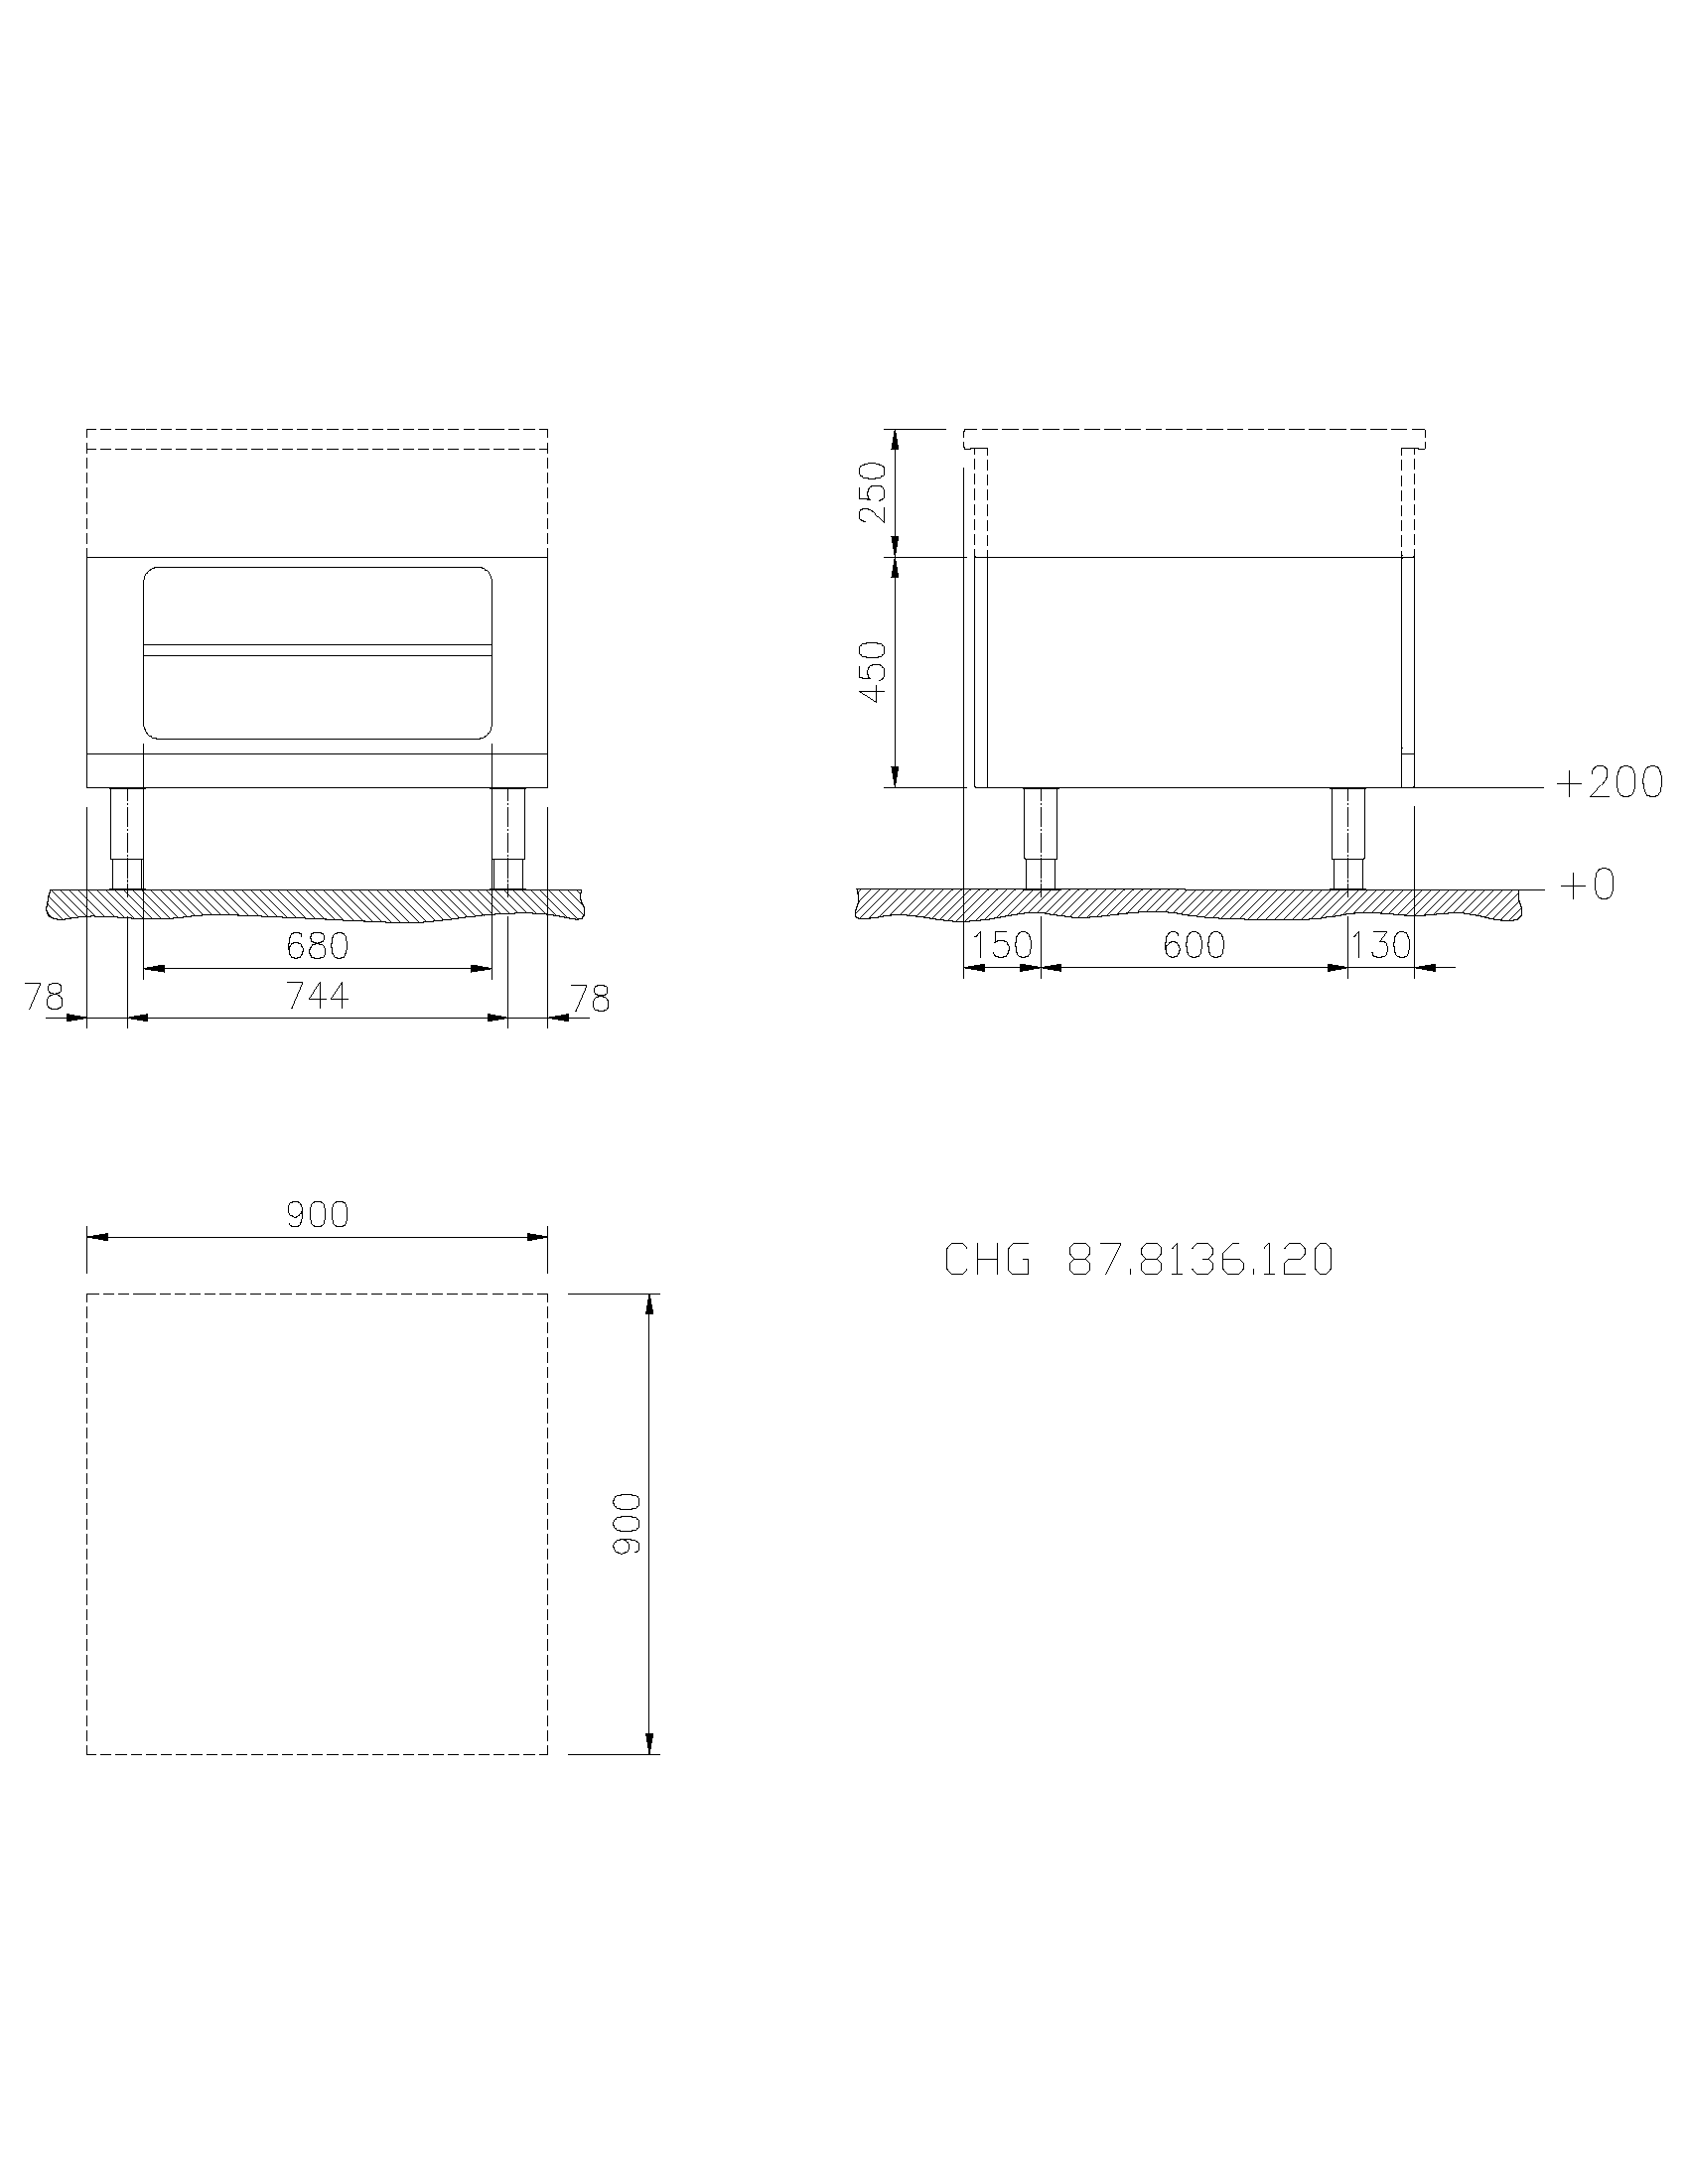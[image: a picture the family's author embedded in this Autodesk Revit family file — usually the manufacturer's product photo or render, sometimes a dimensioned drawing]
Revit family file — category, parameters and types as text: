
# Revit family: QF_ELECTROLUXPROFESSIONAL_589865_MCKCEADDDM
name_source: partatom
category: Specialty Equipment
units: mm (PartAtom-declared; Revit-internal decimal feet)

## family parameters
Always vertical = Yes
Cut with Voids When Loaded = No
Enable Cutting in Views = No
Maintain Annotation Orientation = No
Part Type = Normal
Room Calculation Point = No
Round Connector Dimension = Use Diameter
Shared = No
Work Plane-Based = No

## types (1)
- Standard
    Accessory = No
    Cold Water Size = 1"
    Compressed Air Pressure = 0.00 psi
    Compressed Air Size = 0"
    Compressed Air Volume = 0 GPM
    Condensate Return Size = 0"
    Cycle = 50 Hz
    Default Elevation = 0 mm  [stored 0 ft]
    Depth Actual = 900 mm  [stored 2.95276 ft]
    Description = PASTA COOKER, 1X24,5L, 1-SIDE, 400X900X700H-MARINE
    Direct Waste Size = 1"
    Gas Input Pressure = 0.0
    Gas KW = 0
    Gas Size = 0"
    HP = 8 HP
    Height Actual = 700 mm  [stored 2.29659 ft]
    Hot Water Size = 0"
    Item Number = 589865
    Length Actual = 400 mm  [stored 1.31234 ft]
    Manufacturer = Electrolux Professional
    Model = MCKCEADDDM
    Phase = 3
    Refrigerant Compressor Remote = Yes
    Refrigeration Liquid Line Size = 0 mm  [stored 0 ft]
    Refrigeration Suction Line Size = 0 mm  [stored 0 ft]
    Steam Consumption per Hour = 0
    Steam Supply Maximum Pressure = 0.00 psi
    Steam Supply Minimum Pressure = 0.00 psi
    Steam Supply Size = 0"
    URL = http://www.electroluxprofessional.com
    URL Manufacturer = http://www.electroluxprofessional.com
    Volts = 440 V
    Watts = 0 W
    Weight = 73.00 kg

note: source unit labels omitted for Gas Input Pressure — the stored unit's dimension contradicts the parameter name (converter mislabeling)

note: [stored X ft] marks values corroborated as IEEE doubles in the binary element streams (Revit-internal decimal feet)

## geometry (parser evidence)
native form markers: Blend x4, Sweep x11
no freeform markers — native parametric forms only
